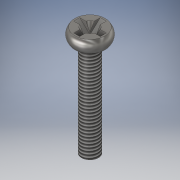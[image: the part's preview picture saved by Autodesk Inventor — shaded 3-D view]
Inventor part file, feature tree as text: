
AUTODESK INVENTOR PART (.ipt)
format: ipt  version: 2019 (Build 230136000, 136)  size: 156,672 bytes
history: native  units: mm
features: sketch x2, revolve x1, extrude x1, pattern_circular x1, thread x1
ambient origin geometry x8: Origin, YZ Plane, XZ Plane, XY Plane, X Axis, Y Axis, Z Axis, Center Point
bodies: Body1 (feature_tree)
feature tree (6):
  revolve  "Вращение1"
  extrude  "Выдавливание2"  Depth=2.8mm
  pattern_circular  "Круговой массив1"  [2 undecoded]
  thread  "Резьба1"
  sketch  "Эскиз3"
  sketch  "Эскиз5"
note: 2 required parameter values undecoded (feature->parameter linkage not recoverable at this tier; creation-order binding heuristic only, values carry confidence <= 0.55)
